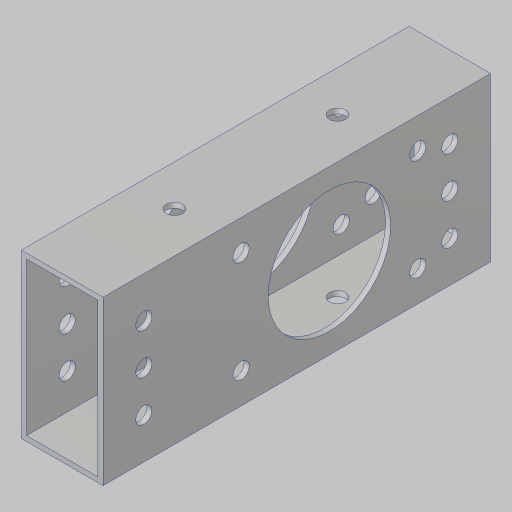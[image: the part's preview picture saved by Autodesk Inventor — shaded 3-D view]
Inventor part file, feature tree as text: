
AUTODESK INVENTOR PART (.ipt)
format: ipt  version: 2023.5 (Build 275446000, 446)  size: 184,320 bytes
history: native  units: in
note: dims shown in document units (in); Inventor stores cm internally (conversion verified against a paired STEP export)
features: extrude x2, sketch x2, hole x2
ambient origin geometry x8: Origin, YZ Plane, XZ Plane, XY Plane, X Axis, Y Axis, Z Axis, Center Point
bodies: Solid1 (feature_tree)
feature tree (6):
  extrude  "Extrusion1"  Depth=2.5in
  sketch  "Sketch2"  dims[d4=0.0in d5=2.5in]
  hole  "Hole1"  [1 undecoded]
  extrude  "Extrusion3"  Depth=2.0in
  hole  "Hole2"  [1 undecoded]
  sketch  "Sketch4"  dims[d10=0.201in d11=0.75in d12=0.385in d13=0.25in d14=0.5635in d15=1.0in d16=0.8108in d17=0.5in d18=0.5in d19=0.5in d23=0.4in d24=2.3622in d26=360.0deg d28=1.5in d29=0.0in d30=0.0in d32=0.201in d33=0.75in d34=0.385in d35=0.25in d36=0.5635in d37=1.0in d38=0.8108in d41=2.0in]
note: 2 required parameter values undecoded (feature->parameter linkage not recoverable at this tier; creation-order binding heuristic only, values carry confidence <= 0.55)
